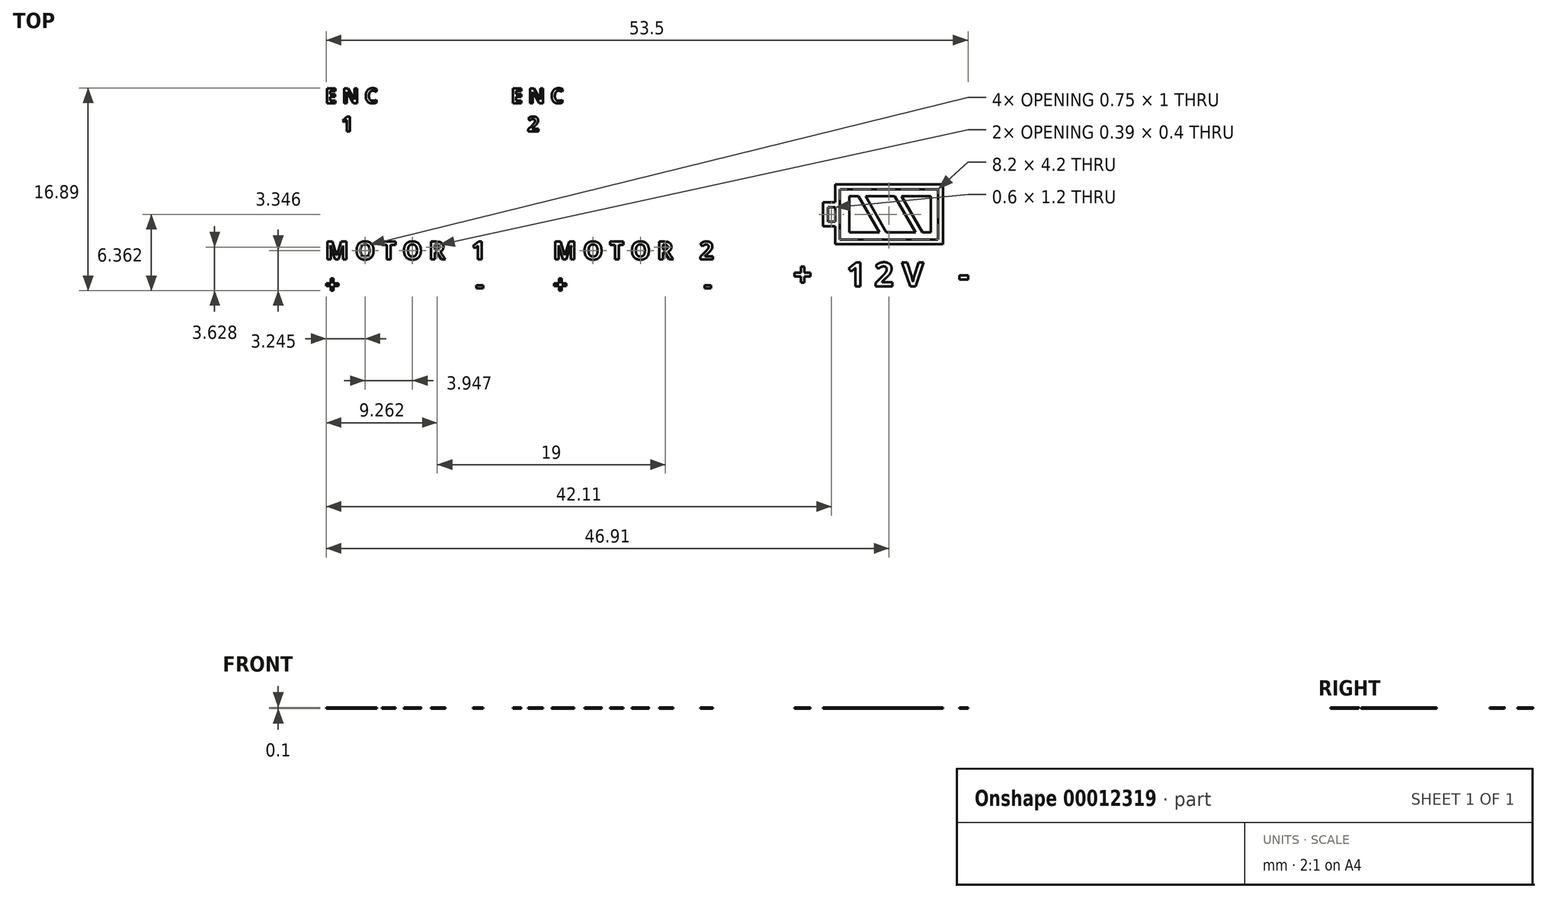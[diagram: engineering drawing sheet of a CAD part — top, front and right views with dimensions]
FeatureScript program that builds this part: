
annotation { "Feature Type Name" : "Feature", "Feature Type Description" : "" }
export const myFeature = defineFeature(function(context is Context, id is Id, definition is map)
    precondition{}
    {
        {
            var Q0;
            Q0=qCreatedBy(makeId("Top.planeOp"),FACE);
            var sketch = newSketch(context, id + "F0", { "sketchPlane" : qUnion([Q0])});
            skText(sketch, "E0", { "text": "E N C\n   1", "fontName": "OpenSans-Bold.ttf"});
            skText(sketch, "E1", { "text": "E N C\n   2", "fontName": "OpenSans-Bold.ttf"});
            skText(sketch, "E2", { "text": "M O T O R    1\n+                     -", "fontName": "OpenSans-Bold.ttf"});
            skText(sketch, "E3", { "text": "M O T O R    2\n+                     -", "fontName": "OpenSans-Bold.ttf"});
            skText(sketch, "E4", { "text": "+    1 2 V    -", "fontName": "OpenSans-Bold.ttf"});
            skLineSegment(sketch, "E5.bottom", {"start": v(42.9, -8.42) * mm, "end": v(51.1, -8.42) * mm});
            skLineSegment(sketch, "E5.top", {"start": v(42.9, -12.62) * mm, "end": v(51.1, -12.62) * mm});
            skLineSegment(sketch, "E5.left", {"start": v(42.9, -8.42) * mm, "end": v(42.9, -12.62) * mm});
            skLineSegment(sketch, "E5.right", {"start": v(51.1, -8.42) * mm, "end": v(51.1, -12.62) * mm});
            skLineSegment(sketch, "E6.rect.bottom", {"start": v(41.9, -9.92) * mm, "end": v(42.5, -9.92) * mm});
            skLineSegment(sketch, "E6.rect.top", {"start": v(41.9, -11.12) * mm, "end": v(42.5, -11.12) * mm});
            skLineSegment(sketch, "E6.rect.left", {"start": v(41.9, -9.92) * mm, "end": v(41.9, -11.12) * mm});
            skPoint(sketch, "E6.rect.middle", {"position": v(42.9, -10.52) * mm});
            skPoint(sketch, "E6.rect.right.start.orphan", {"position": v(43.9, -9.92) * mm});
            skPoint(sketch, "E7.orphan", {"position": v(43.9, -11.12) * mm});
            skLineSegment(sketch, "E8.0", {"start": v(41.5, -11.52) * mm, "end": v(42.5, -11.52) * mm});
            skLineSegment(sketch, "E8.1", {"start": v(41.5, -9.52) * mm, "end": v(41.5, -11.52) * mm});
            skLineSegment(sketch, "E8.2", {"start": v(41.5, -9.52) * mm, "end": v(42.5, -9.52) * mm});
            skLineSegment(sketch, "E9.0", {"start": v(42.5, -8.02) * mm, "end": v(42.5, -9.52) * mm});
            skLineSegment(sketch, "E9.1", {"start": v(42.5, -8.02) * mm, "end": v(51.5, -8.02) * mm});
            skLineSegment(sketch, "E9.2", {"start": v(51.5, -8.02) * mm, "end": v(51.5, -13.02) * mm});
            skLineSegment(sketch, "E9.3", {"start": v(42.5, -13.02) * mm, "end": v(51.5, -13.02) * mm});
            skLineSegment(sketch, "E10.trimOffspring", {"start": v(42.5, -9.92) * mm, "end": v(42.5, -11.12) * mm});
            skLineSegment(sketch, "E11.trimOffspring", {"start": v(42.5, -11.52) * mm, "end": v(42.5, -13.02) * mm});
            skLineSegment(sketch, "E12.rect.bottom", {"start": v(50.5, -9.02) * mm, "end": v(48.05, -9.02) * mm});
            skLineSegment(sketch, "E12.rect.top", {"start": v(50.5, -12.02) * mm, "end": v(49.78, -12.02) * mm});
            skLineSegment(sketch, "E12.rect.left", {"start": v(50.5, -9.02) * mm, "end": v(50.5, -12.02) * mm});
            skLineSegment(sketch, "E12.rect.right", {"start": v(43.7, -9.02) * mm, "end": v(43.7, -12.02) * mm});
            skPoint(sketch, "E12.rect.middle", {"position": v(47.1, -10.52) * mm});
            skLineSegment(sketch, "E13", {"start": v(45.05, -9.02) * mm, "end": v(46.78, -12.02) * mm});
            skLineSegment(sketch, "E14.0", {"start": v(44.47, -9.02) * mm, "end": v(46.2, -12.02) * mm});
            skLineSegment(sketch, "E15.1.0.0", {"start": v(47.47, -9.02) * mm, "end": v(49.2, -12.02) * mm});
            skLineSegment(sketch, "E15.1.0.1", {"start": v(48.05, -9.02) * mm, "end": v(49.78, -12.02) * mm});
            skLineSegment(sketch, "E15.direction1", {"start": v(46.95, -12.02) * mm, "end": v(49.95, -12.02) * mm, "construction": true});
            skLineSegment(sketch, "E16.trimOffspring", {"start": v(44.47, -9.02) * mm, "end": v(43.7, -9.02) * mm});
            skLineSegment(sketch, "E17.trimOffspring", {"start": v(47.47, -9.02) * mm, "end": v(45.05, -9.02) * mm});
            skLineSegment(sketch, "E18.trimOffspring", {"start": v(49.2, -12.02) * mm, "end": v(46.78, -12.02) * mm});
            skLineSegment(sketch, "E19.trimOffspring", {"start": v(46.2, -12.02) * mm, "end": v(43.7, -12.02) * mm});
            const initialGuessF0  = {"E0": [0, -0.00125, 1, 0, 0.00125], "E1": [0.0155, -0.00125, 1, 0, 0.00125], "E2": [0, -0.01428, 1, 0, 0.0015], "E3": [0.019, -0.01428, 1, 0, 0.0015], "E4": [0.039, -0.01652, 1, 0, 0.002]};
            skSetInitialGuess(sketch, initialGuessF0);
            skSolve(sketch);
        }
        {
            var Q0;
            Q0=qSketchRegion(id+"F0",true);
            var Q1;
            Q1=makeQuery(id+"F0.imprint","IMPRINT",FACE,{"disambiguationData":[TD([[makeQuery(id+"F0.imprint","IMPRINT",EDGE,{"derivedFrom":sQuery(id+"F0.wireOp",EDGE,"E12.rect.right")}),1.0]])]});
            var Q2;
            Q2=makeQuery(id+"F0.imprint","IMPRINT",FACE,{"disambiguationData":[TD([[makeQuery(id+"F0.imprint","IMPRINT",EDGE,{"derivedFrom":sQuery(id+"F0.wireOp",EDGE,"E13")}),1.0]])]});
            var Q3;
            Q3=makeQuery(id+"F0.imprint","IMPRINT",FACE,{"disambiguationData":[TD([[makeQuery(id+"F0.imprint","IMPRINT",EDGE,{"derivedFrom":sQuery(id+"F0.wireOp",EDGE,"E12.rect.bottom")}),1.0]])]});
            extrude(context, id + "F1", {"entities" : qUnion([Q0, Q1, Q2, Q3]), "depth" : .1 * mm});
        }
    });
